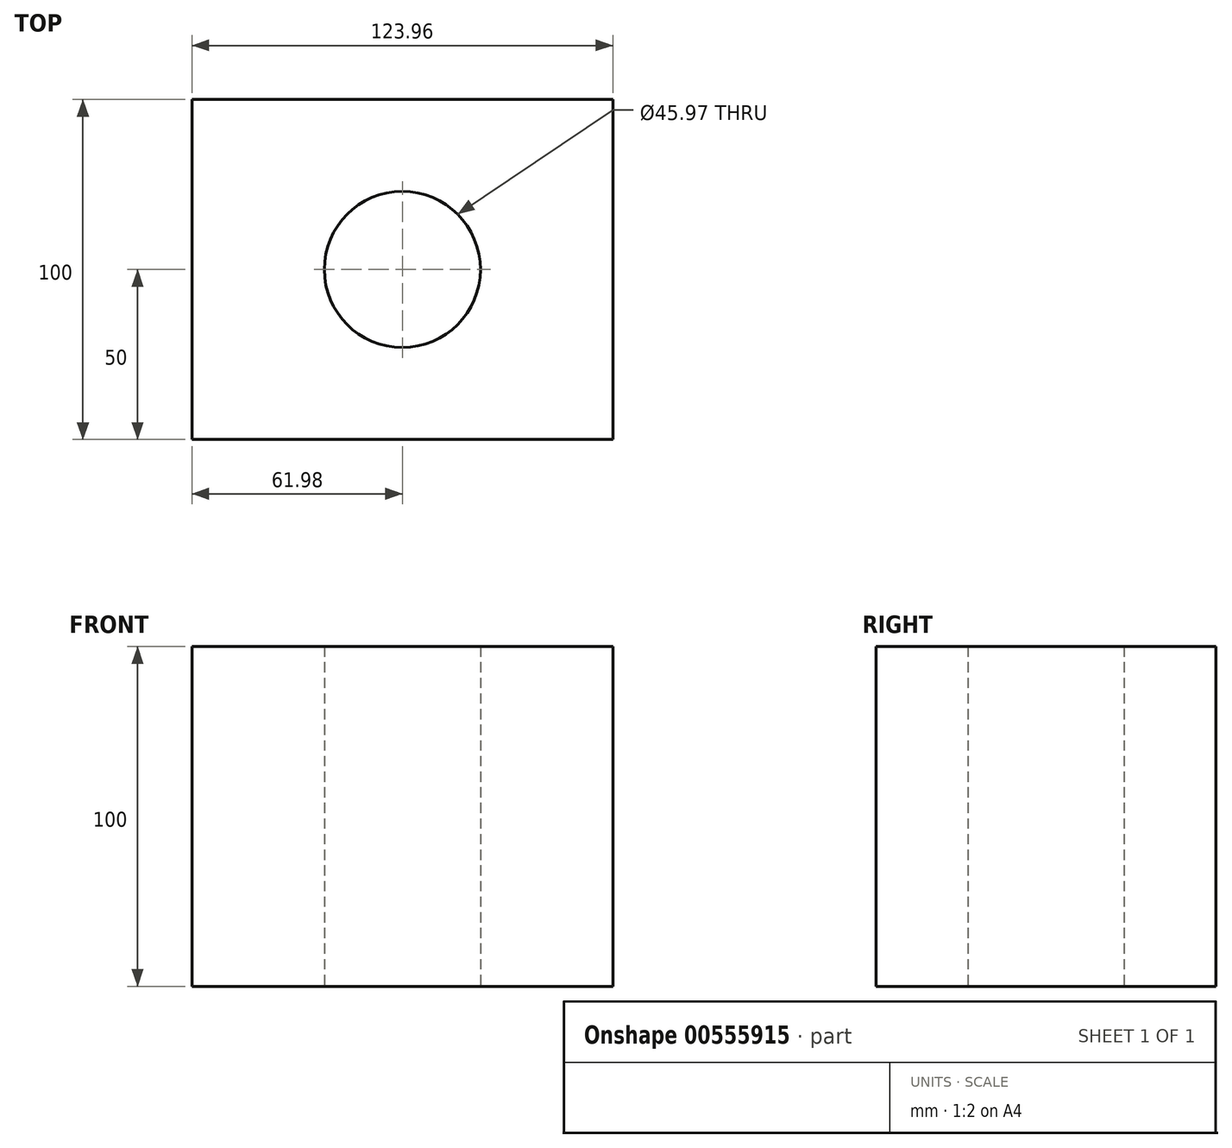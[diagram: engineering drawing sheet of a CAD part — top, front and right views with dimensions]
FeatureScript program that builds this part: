
annotation { "Feature Type Name" : "Feature", "Feature Type Description" : "" }
export const myFeature = defineFeature(function(context is Context, id is Id, definition is map)
    precondition{}
    {
        {
            var Q0;
            Q0=qCreatedBy(makeId("Top.planeOp"),FACE);
            var sketch = newSketch(context, id + "F0", { "sketchPlane" : qUnion([Q0])});
            skLineSegment(sketch, "E0.bottom", {"start": v(61.98, -50) * mm, "end": v(-61.98, -50) * mm});
            skLineSegment(sketch, "E0.top", {"start": v(61.98, 50) * mm, "end": v(-61.98, 50) * mm});
            skLineSegment(sketch, "E0.left", {"start": v(61.98, -50) * mm, "end": v(61.98, 50) * mm});
            skLineSegment(sketch, "E0.right", {"start": v(-61.98, -50) * mm, "end": v(-61.98, 50) * mm});
            skPoint(sketch, "E0.middle", {"position": v(0, 0) * mm});
            skCircle(sketch, "E1", {"center": v(0, 0) * mm, "radius": 22.99 * mm});
            skSolve(sketch);
        }
        {
            var Q0;
            Q0=makeQuery(id+"F0.imprint","IMPRINT",FACE,{"disambiguationData":[TD([[makeQuery(id+"F0.imprint","IMPRINT",EDGE,{"derivedFrom":sQuery(id+"F0.wireOp",EDGE,"E0.bottom")}),-1.0]])]});
            extrude(context, id + "F1", {"entities" : qUnion([Q0]), "depth" : 100 * mm, "offsetDistance" : 25 * mm});
        }
    });
